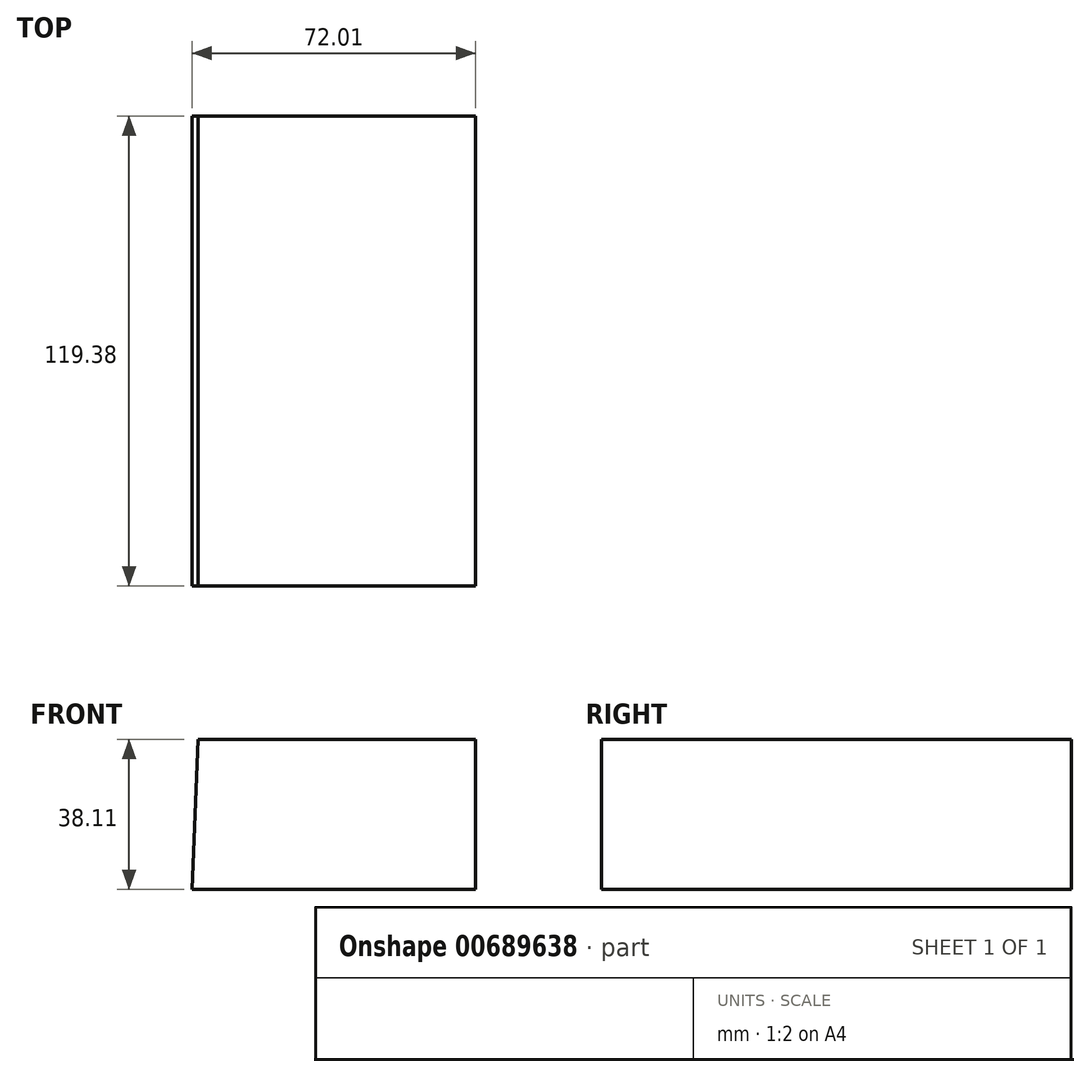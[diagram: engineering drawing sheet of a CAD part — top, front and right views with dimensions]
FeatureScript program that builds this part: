
annotation { "Feature Type Name" : "Feature", "Feature Type Description" : "" }
export const myFeature = defineFeature(function(context is Context, id is Id, definition is map)
    precondition{}
    {
        {
            var Q0;
            Q0=qCreatedBy(makeId("Front.planeOp"),FACE);
            var sketch = newSketch(context, id + "F0", { "sketchPlane" : qUnion([Q0])});
            skLineSegment(sketch, "E0", {"start": v(-49.78, 42.9) * mm, "end": v(20.68, 42.9) * mm});
            skLineSegment(sketch, "E1", {"start": v(20.68, 42.9) * mm, "end": v(20.68, 4.8) * mm});
            skLineSegment(sketch, "E2", {"start": v(20.68, 4.8) * mm, "end": v(-51.33, 4.8) * mm});
            skLineSegment(sketch, "E3", {"start": v(-51.33, 4.8) * mm, "end": v(-49.78, 42.9) * mm});
            skSolve(sketch);
        }
        {
            var Q0;
            Q0 = qSketchRegion(id + "F0", true);
            extrude(context, id + "F1", {"entities" : qUnion([Q0]), "depth" : 119.38 * mm, "offsetDistance" : 25.4 * mm});
        }
    });
